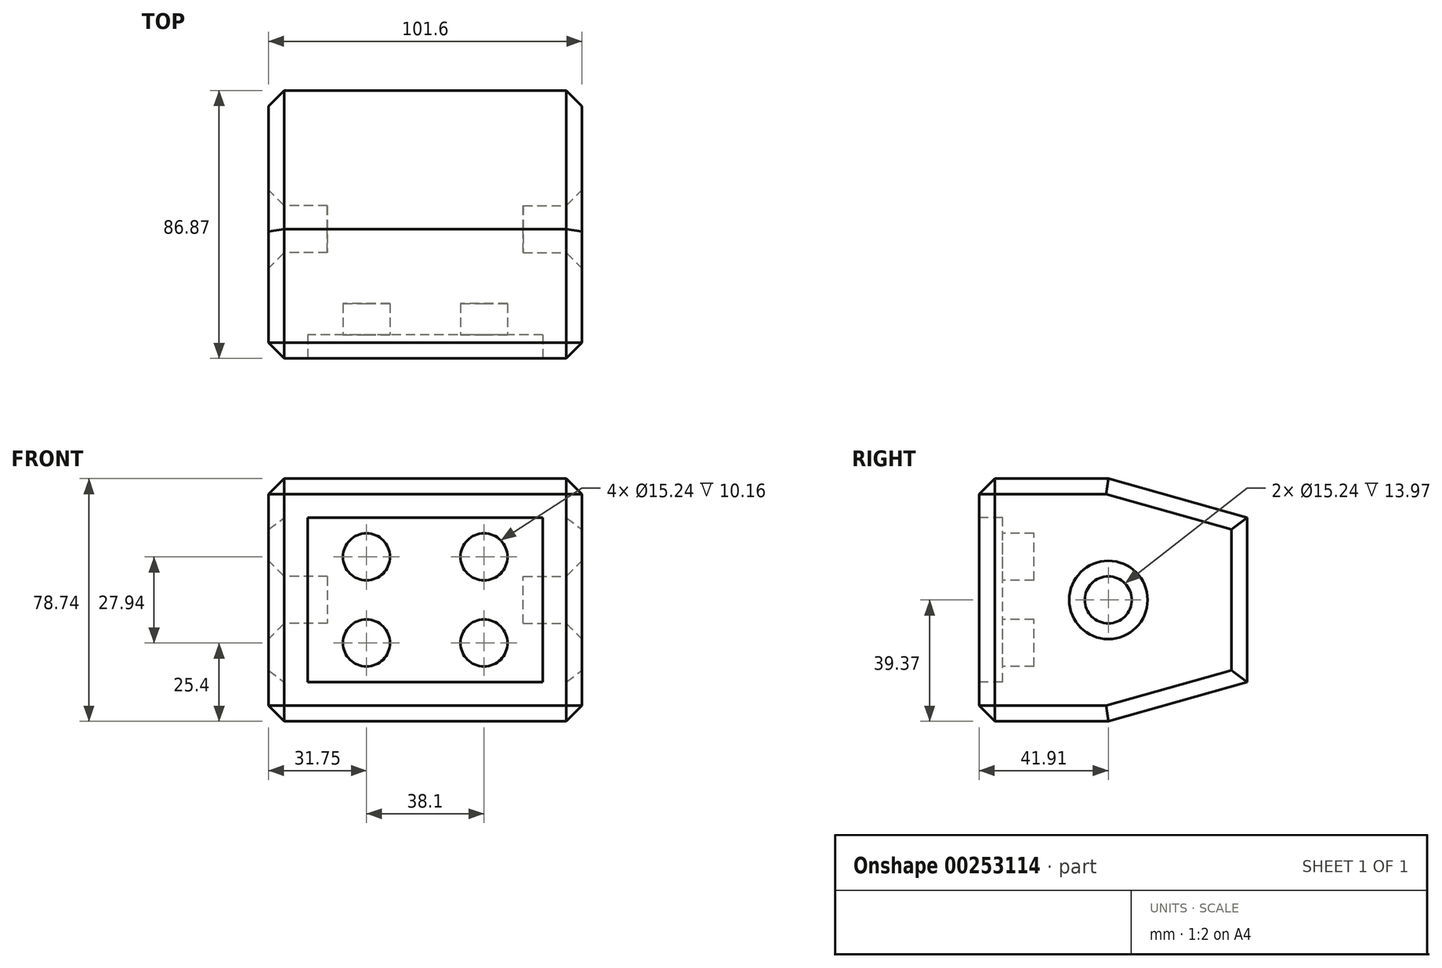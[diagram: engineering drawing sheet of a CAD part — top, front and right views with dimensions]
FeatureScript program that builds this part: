
annotation { "Feature Type Name" : "Feature", "Feature Type Description" : "" }
export const myFeature = defineFeature(function(context is Context, id is Id, definition is map)
    precondition{}
    {
        {
            var Q0;
            Q0=qCreatedBy(makeId("Right.planeOp"),FACE);
            var sketch = newSketch(context, id + "F0", { "sketchPlane" : qUnion([Q0])});
            skLineSegment(sketch, "E0", {"start": v(0, 0) * mm, "end": v(37.96, 0) * mm, "construction": true});
            skLineSegment(sketch, "E1", {"start": v(0, 0) * mm, "end": v(60.44, 0) * mm, "construction": true});
            skLineSegment(sketch, "E2", {"start": v(0, 39.37) * mm, "end": v(41.91, 39.37) * mm});
            skLineSegment(sketch, "E3", {"start": v(0, 39.37) * mm, "end": v(0, 0) * mm});
            skLineSegment(sketch, "E4.MirrorCS", {"start": v(0, -39.37) * mm, "end": v(41.91, -39.37) * mm});
            skLineSegment(sketch, "E5.MirrorCS", {"start": v(0, -39.37) * mm, "end": v(0, 0) * mm});
            skLineSegment(sketch, "E6", {"start": v(41.9, 39.37) * mm, "end": v(86.87, 26.67) * mm});
            skLineSegment(sketch, "E7", {"start": v(86.87, 26.67) * mm, "end": v(86.87, 0) * mm});
            skLineSegment(sketch, "E8.MirrorCS", {"start": v(41.9, -39.37) * mm, "end": v(86.87, -26.67) * mm});
            skLineSegment(sketch, "E9.MirrorCS", {"start": v(86.87, -26.67) * mm, "end": v(86.87, 0) * mm});
            skSolve(sketch);
        }
        {
            var Q0;
            Q0 = qSketchRegion(id + "F0", true);
            extrude(context, id + "F1", {"entities" : qUnion([Q0]), "endBound" : BoundingType.SYMMETRIC, "depth" : 101.6 * mm});
        }
        {
            var Q0;
            Q0=makeQuery(id+"F1.opExtrude","SWEPT_FACE",FACE,{"disambiguationData":[OSD([sQuery(id+"F0.wireOp",EDGE,"E3"),sQuery(id+"F0.wireOp",EDGE,"E5.MirrorCS")])]});
            var sketch = newSketch(context, id + "F2", { "sketchPlane" : qUnion([Q0])});
            skLineSegment(sketch, "E10.bottom", {"start": v(38.1, -26.67) * mm, "end": v(-38.1, -26.67) * mm});
            skLineSegment(sketch, "E10.top", {"start": v(38.1, 26.67) * mm, "end": v(-38.1, 26.67) * mm});
            skLineSegment(sketch, "E10.left", {"start": v(38.1, -26.67) * mm, "end": v(38.1, 26.67) * mm});
            skLineSegment(sketch, "E10.right", {"start": v(-38.1, -26.67) * mm, "end": v(-38.1, 26.67) * mm});
            skPoint(sketch, "E10.middle", {"position": v(0, 0) * mm});
            skSolve(sketch);
        }
        {
            var Q0;
            Q0 = qSketchRegion(id + "F2", true);
            extrude(context, id + "F3", {"entities" : qUnion([Q0]), "operationType" : NewBodyOperationType.REMOVE, "oppositeDirection" : true, "depth" : 7.62 * mm});
        }
        {
            var Q0;
            Q0=makeQuery(id+"F3.boolean.opBoolean","COPY",FACE,{"derivedFrom":makeQuery(id+"F3.opExtrude","CAP_FACE",FACE,{"disambiguationData":[OSD([sQuery(id+"F2.wireOp",EDGE,"E10.bottom"),sQuery(id+"F2.wireOp",EDGE,"E10.top"),sQuery(id+"F2.wireOp",EDGE,"E10.left"),sQuery(id+"F2.wireOp",EDGE,"E10.right")])],"isStart":false})});
            var sketch = newSketch(context, id + "F4", { "sketchPlane" : qUnion([Q0])});
            skCircle(sketch, "E11", {"center": v(-19.05, 13.97) * mm, "radius": 7.62 * mm});
            skCircle(sketch, "E12", {"center": v(19.05, 13.97) * mm, "radius": 7.62 * mm});
            skCircle(sketch, "E13", {"center": v(-19.05, -13.97) * mm, "radius": 7.62 * mm});
            skCircle(sketch, "E14", {"center": v(19.05, -13.97) * mm, "radius": 7.62 * mm});
            skSolve(sketch);
        }
        {
            var Q0;
            Q0 = qSketchRegion(id + "F4", true);
            extrude(context, id + "F5", {"entities" : qUnion([Q0]), "operationType" : NewBodyOperationType.REMOVE, "oppositeDirection" : true, "depth" : 10.16 * mm});
        }
        {
            var Q0;
            Q0=makeQuery(id+"F1.opExtrude","CAP_FACE",FACE,{"disambiguationData":[OSD([sQuery(id+"F0.wireOp",EDGE,"E2"),sQuery(id+"F0.wireOp",EDGE,"E3"),sQuery(id+"F0.wireOp",EDGE,"E4.MirrorCS"),sQuery(id+"F0.wireOp",EDGE,"E5.MirrorCS"),sQuery(id+"F0.wireOp",EDGE,"E6"),sQuery(id+"F0.wireOp",EDGE,"E7"),sQuery(id+"F0.wireOp",EDGE,"E8.MirrorCS"),sQuery(id+"F0.wireOp",EDGE,"E9.MirrorCS")])],"isStart":false});
            var sketch = newSketch(context, id + "F6", { "sketchPlane" : qUnion([Q0])});
            skLineSegment(sketch, "E15", {"start": v(41.91, 39.37) * mm, "end": v(41.91, -39.37) * mm, "construction": true});
            skCircle(sketch, "E16", {"center": v(41.91, 0) * mm, "radius": 7.62 * mm});
            skSolve(sketch);
        }
        {
            var Q0;
            Q0 = qSketchRegion(id + "F6", true);
            extrude(context, id + "F7", {"entities" : qUnion([Q0]), "operationType" : NewBodyOperationType.REMOVE, "oppositeDirection" : true, "depth" : 19.05 * mm});
        }
        {
            var Q0;
            Q0=makeQuery(id+"F1.opExtrude","CAP_FACE",FACE,{"disambiguationData":[OSD([sQuery(id+"F0.wireOp",EDGE,"E2"),sQuery(id+"F0.wireOp",EDGE,"E3"),sQuery(id+"F0.wireOp",EDGE,"E4.MirrorCS"),sQuery(id+"F0.wireOp",EDGE,"E5.MirrorCS"),sQuery(id+"F0.wireOp",EDGE,"E6"),sQuery(id+"F0.wireOp",EDGE,"E7"),sQuery(id+"F0.wireOp",EDGE,"E8.MirrorCS"),sQuery(id+"F0.wireOp",EDGE,"E9.MirrorCS")])],"isStart":true});
            var sketch = newSketch(context, id + "F8", { "sketchPlane" : qUnion([Q0])});
            skLineSegment(sketch, "E17", {"start": v(-41.91, 39.37) * mm, "end": v(-41.91, -39.37) * mm, "construction": true});
            skCircle(sketch, "E18", {"center": v(-41.91, 0) * mm, "radius": 7.62 * mm});
            skSolve(sketch);
        }
        {
            var Q0;
            Q0 = qSketchRegion(id + "F8", true);
            extrude(context, id + "F9", {"entities" : qUnion([Q0]), "operationType" : NewBodyOperationType.REMOVE, "oppositeDirection" : true, "depth" : 19.05 * mm});
        }
        {
            var Q0;
            Q0=makeQuery(id+"F1.opExtrude","CAP_FACE",FACE,{"disambiguationData":[OSD([sQuery(id+"F0.wireOp",EDGE,"E2"),sQuery(id+"F0.wireOp",EDGE,"E3"),sQuery(id+"F0.wireOp",EDGE,"E4.MirrorCS"),sQuery(id+"F0.wireOp",EDGE,"E5.MirrorCS"),sQuery(id+"F0.wireOp",EDGE,"E6"),sQuery(id+"F0.wireOp",EDGE,"E7"),sQuery(id+"F0.wireOp",EDGE,"E8.MirrorCS"),sQuery(id+"F0.wireOp",EDGE,"E9.MirrorCS")])],"isStart":false});
            var Q1;
            Q1=makeQuery(id+"F1.opExtrude","CAP_FACE",FACE,{"disambiguationData":[OSD([sQuery(id+"F0.wireOp",EDGE,"E2"),sQuery(id+"F0.wireOp",EDGE,"E3"),sQuery(id+"F0.wireOp",EDGE,"E4.MirrorCS"),sQuery(id+"F0.wireOp",EDGE,"E5.MirrorCS"),sQuery(id+"F0.wireOp",EDGE,"E6"),sQuery(id+"F0.wireOp",EDGE,"E7"),sQuery(id+"F0.wireOp",EDGE,"E8.MirrorCS"),sQuery(id+"F0.wireOp",EDGE,"E9.MirrorCS")])],"isStart":true});
            var Q2;
            Q2=makeQuery(id+"F1.opExtrude","SWEPT_EDGE",EDGE,{"disambiguationData":[OSD([sQuery(id+"F0.wireOp",EDGE,"E2"),sQuery(id+"F0.wireOp",EDGE,"E3")])]});
            var Q3;
            Q3=makeQuery(id+"F1.opExtrude","SWEPT_EDGE",EDGE,{"disambiguationData":[OSD([sQuery(id+"F0.wireOp",EDGE,"E4.MirrorCS"),sQuery(id+"F0.wireOp",EDGE,"E5.MirrorCS")])]});
            chamfer(context, id + "F10", {"entities" : qUnion([Q0, Q1, Q2, Q3]), "width" : 5.08 * mm, "tangentPropagation" : true});
        }
    });
